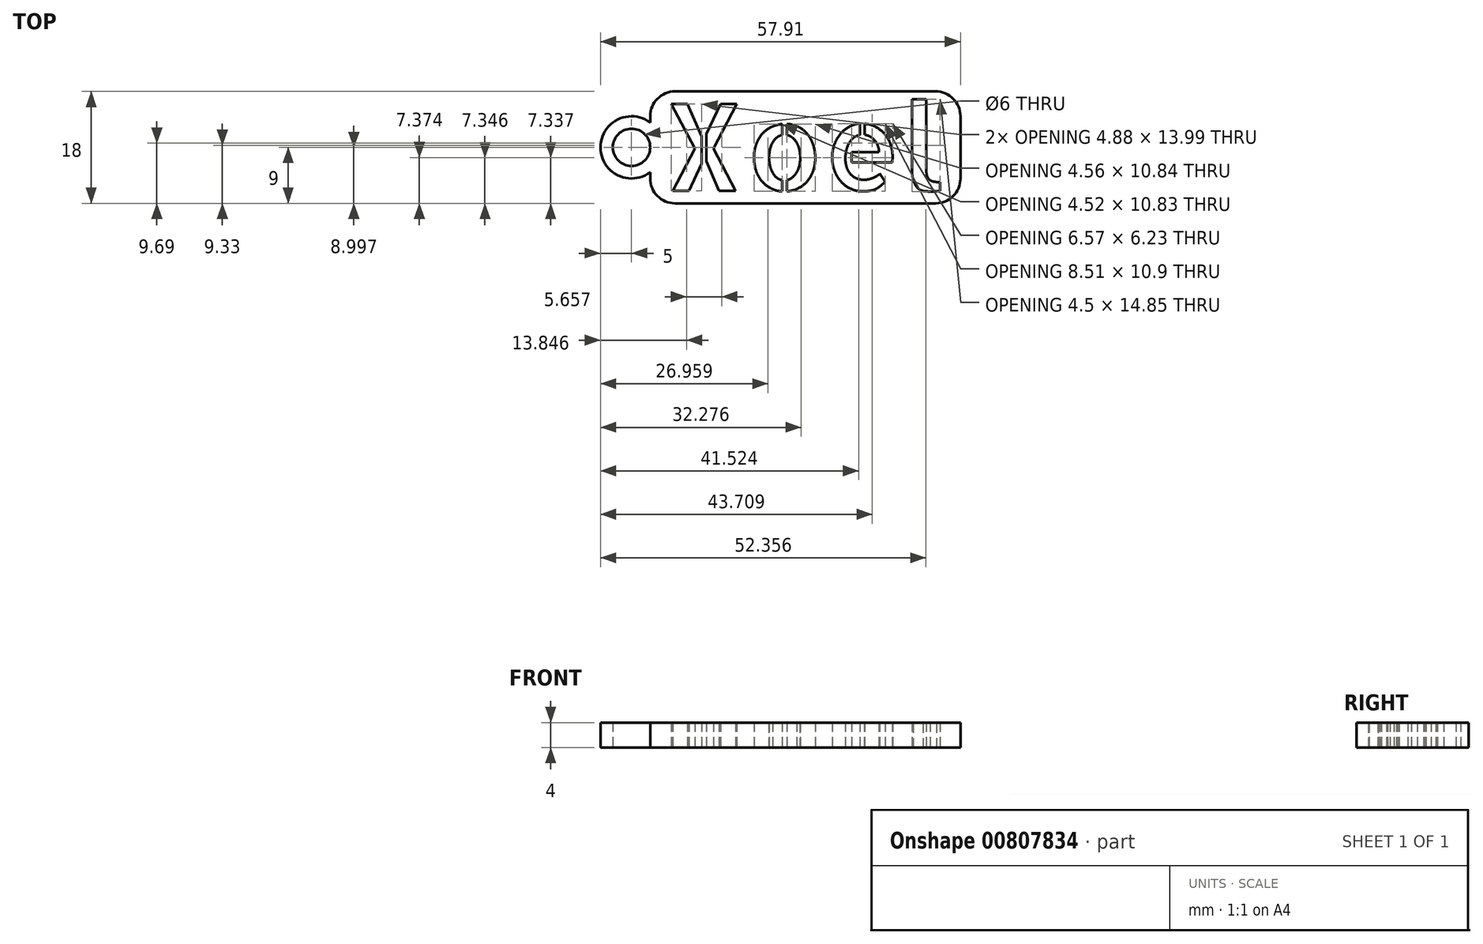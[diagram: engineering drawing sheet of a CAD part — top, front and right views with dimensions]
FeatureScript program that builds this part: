
annotation { "Feature Type Name" : "Feature", "Feature Type Description" : "" }
export const myFeature = defineFeature(function(context is Context, id is Id, definition is map)
    precondition{}
    {
        {
            var Q0;
            Q0=qCreatedBy(makeId("Top.planeOp"),FACE);
            var sketch = newSketch(context, id + "F0", { "sketchPlane" : qUnion([Q0])});
            skLineSegment(sketch, "E0.bottom", {"start": v(-2, -2) * mm, "end": v(47.9, -2) * mm});
            skLineSegment(sketch, "E0.top", {"start": v(-2, 16) * mm, "end": v(47.9, 16) * mm});
            skLineSegment(sketch, "E0.left", {"start": v(-2, -2) * mm, "end": v(-2, 3) * mm});
            skLineSegment(sketch, "E0.right", {"start": v(47.9, -2) * mm, "end": v(47.9, 16) * mm});
            skArc(sketch, "E1", {"start": v(-2, 11) * mm, "mid": v(-10, 7) * mm, "end": v(-2, 3) * mm});
            skLineSegment(sketch, "E2.trimOffspring", {"start": v(-2, 11) * mm, "end": v(-2, 16) * mm});
            skCircle(sketch, "E3", {"center": v(-5, 7) * mm, "radius": 3 * mm});
            skLineSegment(sketch, "E4", {"start": v(47.9, 7) * mm, "end": v(-10, 7) * mm, "construction": true});
            skText(sketch, "E5", { "text": "Xoel", "fontName": "AllertaStencil-Regular.ttf"});
            const initialGuessF0  = {"E5": [0, 0, 1, 0, 0.014]};
            skSetInitialGuess(sketch, initialGuessF0);
            skSolve(sketch);
        }
        {
            var Q0;
            Q0=makeQuery(id+"F0.imprint","IMPRINT",FACE,{"disambiguationData":[TD([[makeQuery(id+"F0.imprint","IMPRINT",EDGE,{"derivedFrom":sQuery(id+"F0.wireOp",EDGE,"E0.bottom")}),1.0]])]});
            extrude(context, id + "F1", {"entities" : qUnion([Q0]), "depth" : 4 * mm, "offsetDistance" : 25 * mm});
        }
        {
            var Q0;
            Q0=makeQuery(id+"F1.opExtrude","SWEPT_EDGE",EDGE,{"disambiguationData":[OSD([sQuery(id+"F0.wireOp",EDGE,"E0.bottom"),sQuery(id+"F0.wireOp",EDGE,"E0.left")])]});
            var Q1;
            Q1=makeQuery(id+"F1.opExtrude","SWEPT_EDGE",EDGE,{"disambiguationData":[OSD([sQuery(id+"F0.wireOp",EDGE,"E0.bottom"),sQuery(id+"F0.wireOp",EDGE,"E0.right")])]});
            var Q2;
            Q2=makeQuery(id+"F1.opExtrude","SWEPT_EDGE",EDGE,{"disambiguationData":[OSD([sQuery(id+"F0.wireOp",EDGE,"E0.top"),sQuery(id+"F0.wireOp",EDGE,"E0.right")])]});
            var Q3;
            Q3=makeQuery(id+"F1.opExtrude","SWEPT_EDGE",EDGE,{"disambiguationData":[OSD([sQuery(id+"F0.wireOp",EDGE,"E0.top"),sQuery(id+"F0.wireOp",EDGE,"E2.trimOffspring")])]});
            fillet(context, id + "F2", {"entities" : qUnion([Q0, Q1, Q2, Q3]), "radius" : 4 * mm, "tangentPropagation" : true, "allowEdgeOverflow" : false});
        }
    });
